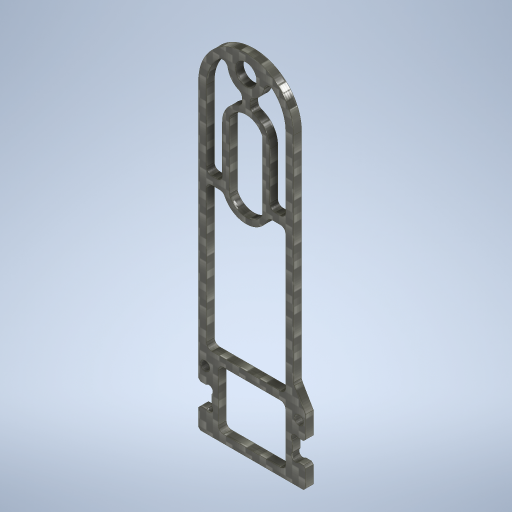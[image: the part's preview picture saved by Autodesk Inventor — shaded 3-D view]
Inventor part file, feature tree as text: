
AUTODESK INVENTOR PART (.ipt)
format: ipt  version: 2024.2 (Build 282272000, 272)  size: 541,696 bytes
history: native  units: mm
features: hole x2, sketch x1, extrude x1, chamfer x1
ambient origin geometry x8: Origin, YZ Plane, XZ Plane, XY Plane, X Axis, Y Axis, Z Axis, Center Point
bodies: Solid1 (feature_tree)
feature tree (5):
  sketch  "Sketch1"  dims[d2=12.5mm d3=60.0deg d4=20.0mm d5=20.0mm d6=20.0mm d12=17.320508mm d13=120.0mm d14=30.0deg d15=5.0mm d17=32.5mm d18=43.0mm d19=9.5mm d21=0.05mm d24=3.0mm d25=9.0mm d26=6.0mm d27=3.0mm d28=0.0mm d29=8.0mm d30=6.0mm d31=4.0mm d32=2.0mm d33=90.0deg d34=8.0mm d35=20.594885mm d36=8.0mm d38=8.1mm d39=3.5mm d40=3.5mm d41=6.0mm d42=4.0mm d43=2.0mm d44=90.0deg d45=8.0mm d46=20.594885mm d48=50.0mm d50=3.0mm d51=3.5mm d56=8.8mm d57=5.0mm d58=1.85mm d59=1.85mm d60=2.0mm d65=14.0mm d66=30.0deg d70=3.0mm d74=3.0mm d81=7.0mm d82=5.0mm d85=5.0mm d86=2.5mm d88=0.75mm d89=2.0mm d90=45.0deg d91=8.0mm d92=8.0mm d93=3.0mm d95=3.0mm d96=3.0mm d97=9.0mm d99=1.5mm]
  extrude  "Extrusion1"  TaperAngle=60.0deg  [1 undecoded]
  hole  "Phi8.0-H7"  [1 undecoded]
  hole  "Phi3.5"  [1 undecoded]
  chamfer  "C0.5"  Distance=20.0mm
note: 3 required parameter values undecoded (feature->parameter linkage not recoverable at this tier; creation-order binding heuristic only, values carry confidence <= 0.55)
